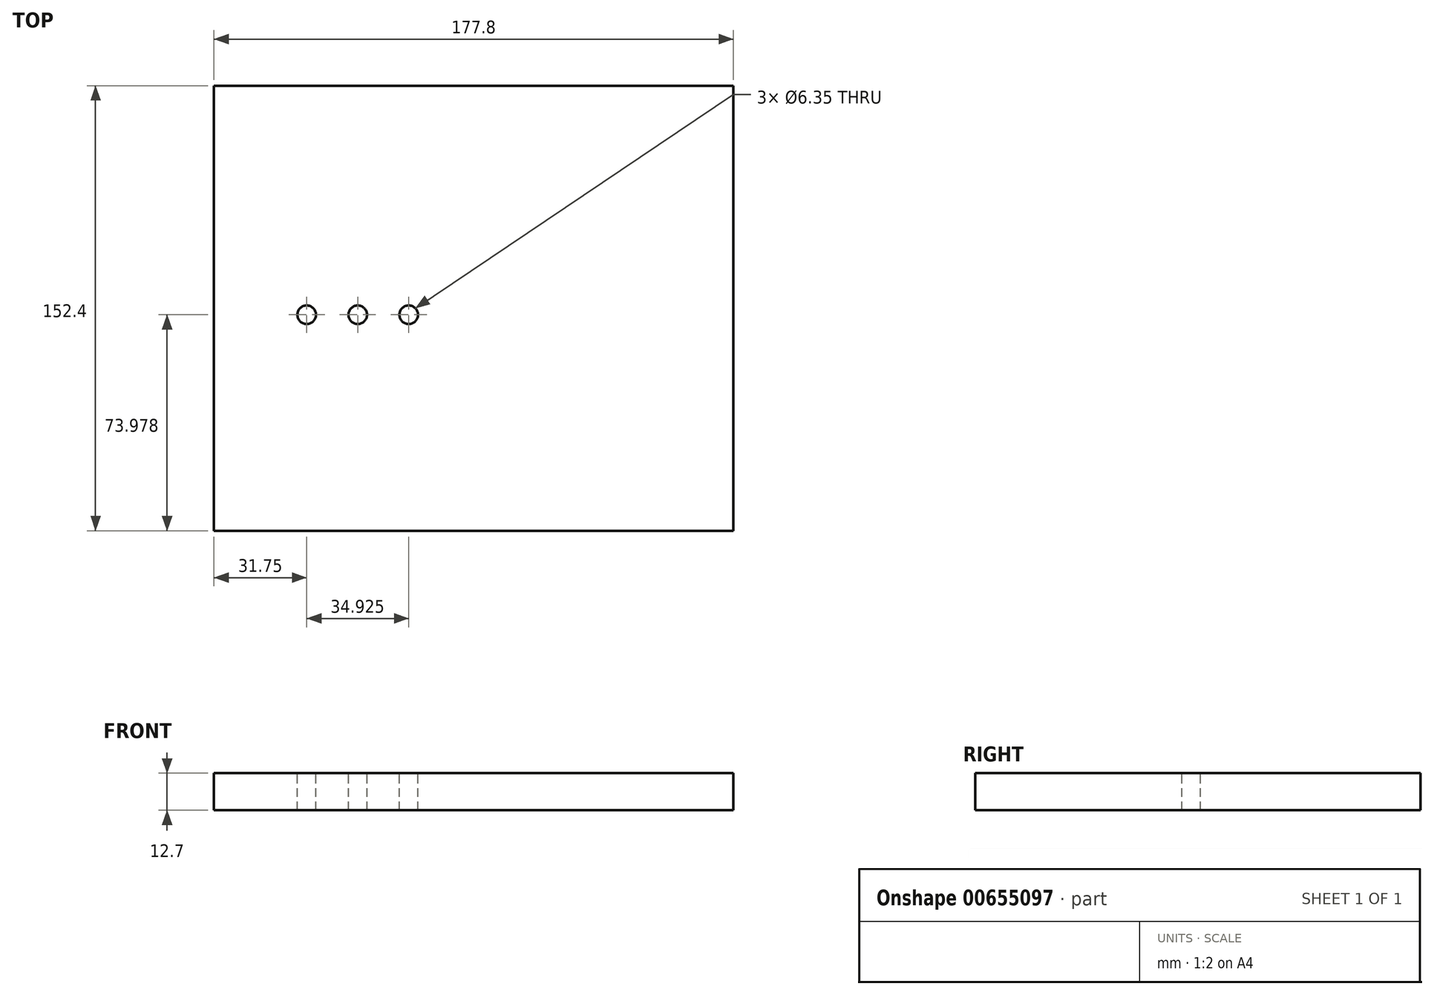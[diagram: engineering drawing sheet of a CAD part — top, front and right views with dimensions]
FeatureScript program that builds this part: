
annotation { "Feature Type Name" : "Feature", "Feature Type Description" : "" }
export const myFeature = defineFeature(function(context is Context, id is Id, definition is map)
    precondition{}
    {
        {
            var Q0;
            Q0=qCreatedBy(makeId("Top.planeOp"),FACE);
            var sketch = newSketch(context, id + "F0", { "sketchPlane" : qUnion([Q0])});
            skLineSegment(sketch, "E0.bottom", {"start": v(-76.2, 76.2) * mm, "end": v(101.6, 76.2) * mm});
            skLineSegment(sketch, "E0.top", {"start": v(-76.2, -76.2) * mm, "end": v(101.6, -76.2) * mm});
            skLineSegment(sketch, "E0.left", {"start": v(-76.2, 76.2) * mm, "end": v(-76.2, -76.2) * mm});
            skLineSegment(sketch, "E0.right", {"start": v(101.6, 76.2) * mm, "end": v(101.6, -76.2) * mm});
            skSolve(sketch);
        }
        {
            var Q0;
            Q0 = qSketchRegion(id + "F0", true);
            extrude(context, id + "F1", {"entities" : qUnion([Q0]), "depth" : 6.35 * mm, "offsetDistance" : 25.4 * mm, "hasSecondDirection" : true, "secondDirectionOppositeDirection" : true, "secondDirectionDepth" : 6.35 * mm});
        }
        {
            var Q0;
            Q0=makeQuery(id+"F1.opExtrude","CAP_FACE",FACE,{"disambiguationData":[OSD([sQuery(id+"F0.wireOp",EDGE,"E0.bottom"),sQuery(id+"F0.wireOp",EDGE,"E0.top"),sQuery(id+"F0.wireOp",EDGE,"E0.left"),sQuery(id+"F0.wireOp",EDGE,"E0.right")])],"isStart":false});
            var sketch = newSketch(context, id + "F2", { "sketchPlane" : qUnion([Q0])});
            skCircle(sketch, "E1", {"center": v(-44.45, -2.22) * mm, "radius": 3.18 * mm});
            skLineSegment(sketch, "E2", {"start": v(-76.2, -2.22) * mm, "end": v(-47.62, -2.22) * mm});
            skLineSegment(sketch, "E3.trimOffspring", {"start": v(-41.28, -2.22) * mm, "end": v(-30.16, -2.22) * mm});
            skCircle(sketch, "E4", {"center": v(-26.99, -2.22) * mm, "radius": 3.18 * mm});
            skCircle(sketch, "E5", {"center": v(-9.53, -2.22) * mm, "radius": 3.18 * mm});
            skLineSegment(sketch, "E6.trimOffspring", {"start": v(-23.81, -2.22) * mm, "end": v(-12.7, -2.22) * mm});
            skLineSegment(sketch, "E7.trimOffspring", {"start": v(-6.35, -2.22) * mm, "end": v(101.6, -2.22) * mm});
            skSolve(sketch);
        }
        {
            var Q0;
            Q0 = qSketchRegion(id + "F2", true);
            extrude(context, id + "F3", {"entities" : qUnion([Q0]), "operationType" : NewBodyOperationType.REMOVE, "endBound" : BoundingType.THROUGH_ALL, "oppositeDirection" : true, "depth" : 25.4 * mm, "offsetDistance" : 25.4 * mm});
        }
    });
